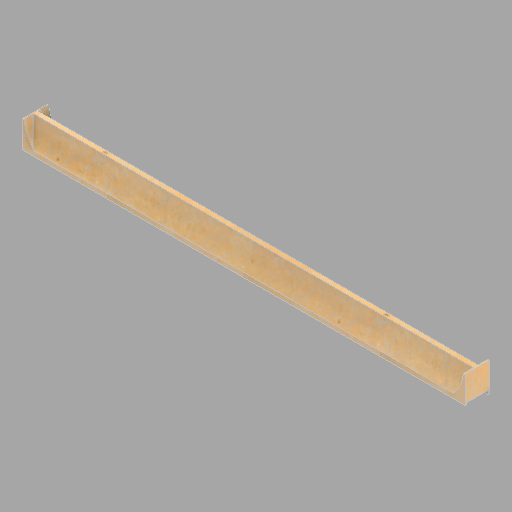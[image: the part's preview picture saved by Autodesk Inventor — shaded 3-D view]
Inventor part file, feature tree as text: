
AUTODESK INVENTOR PART (.ipt)
format: ipt  version: 2022.2 (Build 262287010, 287A)  size: 177,152 bytes
history: native  units: in
note: dims shown in document units (in); Inventor stores cm internally (conversion verified against a paired STEP export)
features: direct_edit x1, revolve x1
ambient origin geometry x8: Origin, YZ Plane, XZ Plane, XY Plane, X Axis, Y Axis, Z Axis, Center Point
bodies: Solid1 (feature_tree), Body1 (feature_tree)
feature tree (2):
  direct_edit  "Direct Edit1"
  revolve  "Rotate1"  Angle=180.0deg
